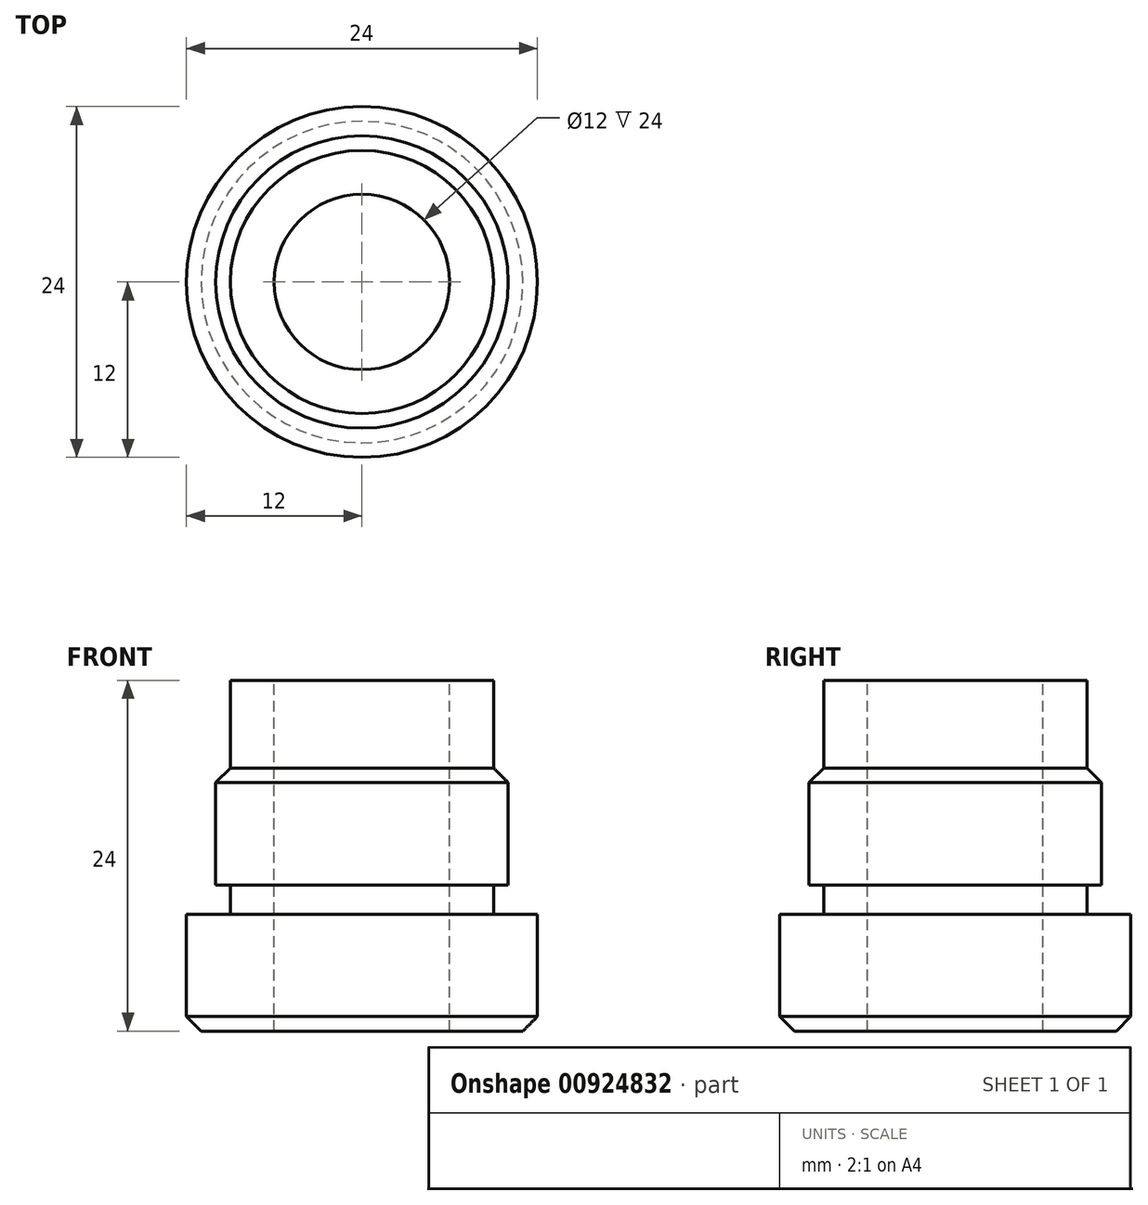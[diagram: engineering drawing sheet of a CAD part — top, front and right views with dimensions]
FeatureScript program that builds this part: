
annotation { "Feature Type Name" : "Feature", "Feature Type Description" : "" }
export const myFeature = defineFeature(function(context is Context, id is Id, definition is map)
    precondition{}
    {
        {
            var Q0;
            Q0=qCreatedBy(makeId("Top.planeOp"),FACE);
            var sketch = newSketch(context, id + "F0", { "sketchPlane" : qUnion([Q0])});
            skCircle(sketch, "E0", {"center": v(0, 0) * mm, "radius": 12 * mm});
            skSolve(sketch);
        }
        {
            var Q0;
            Q0 = qSketchRegion(id + "F0", true);
            extrude(context, id + "F1", {"entities" : qUnion([Q0]), "depth" : 8 * mm, "offsetDistance" : 25 * mm});
        }
        {
            var Q0;
            Q0=makeQuery(id+"F1.opExtrude","CAP_FACE",FACE,{"disambiguationData":[OSD([sQuery(id+"F0.wireOp",EDGE,"E0")])],"isStart":false});
            var sketch = newSketch(context, id + "F2", { "sketchPlane" : qUnion([Q0])});
            skCircle(sketch, "E1", {"center": v(0, 0) * mm, "radius": 10 * mm});
            skSolve(sketch);
        }
        {
            var Q0;
            Q0 = qSketchRegion(id + "F2", true);
            extrude(context, id + "F3", {"entities" : qUnion([Q0]), "operationType" : NewBodyOperationType.ADD, "depth" : 10 * mm, "offsetDistance" : 25 * mm});
        }
        {
            var Q0;
            Q0=makeQuery(id+"F3.opExtrude","CAP_FACE",FACE,{"disambiguationData":[OSD([sQuery(id+"F2.wireOp",EDGE,"E1")])],"isStart":false});
            var sketch = newSketch(context, id + "F4", { "sketchPlane" : qUnion([Q0])});
            skCircle(sketch, "E2", {"center": v(0, 0) * mm, "radius": 9 * mm});
            skSolve(sketch);
        }
        {
            var Q0;
            Q0 = qSketchRegion(id + "F4", true);
            extrude(context, id + "F5", {"entities" : qUnion([Q0]), "operationType" : NewBodyOperationType.ADD, "depth" : 6 * mm, "offsetDistance" : 25 * mm});
        }
        {
            var Q0;
            Q0=qCreatedBy(makeId("Right.planeOp"),FACE);
            var sketch = newSketch(context, id + "F6", { "sketchPlane" : qUnion([Q0])});
            skLineSegment(sketch, "E3.bottom", {"start": v(10, 8) * mm, "end": v(9, 8) * mm});
            skLineSegment(sketch, "E3.top", {"start": v(10, 10) * mm, "end": v(9, 10) * mm});
            skLineSegment(sketch, "E3.left", {"start": v(10, 8) * mm, "end": v(10, 10) * mm});
            skLineSegment(sketch, "E3.right", {"start": v(9, 8) * mm, "end": v(9, 10) * mm});
            skSolve(sketch);
        }
        {
            var Q0;
            Q0=qCreatedBy(makeId("Front.planeOp"),FACE);
            var sketch = newSketch(context, id + "F7", { "sketchPlane" : qUnion([Q0])});
            skLineSegment(sketch, "E4", {"start": v(0, 0) * mm, "end": v(0, 27.45) * mm, "construction": true});
            skSolve(sketch);
        }
        {
            var Q0;
            Q0 = qSketchRegion(id + "F6", true);
            var Q1;
            Q1=sQuery(id+"F7.wireOp",EDGE,"E4");
            revolve(context, id + "F8", {"operationType" : NewBodyOperationType.REMOVE, "surfaceOperationType" : NewSurfaceOperationType.NEW, "entities" : qUnion([Q0]), "axis" : qUnion([Q1]), "revolveType" : RevolveType.FULL, "oppositeDirection" : true});
        }
        {
            var Q0;
            Q0=makeQuery(id+"F1.opExtrude","CAP_EDGE",EDGE,{"disambiguationData":[OSD([sQuery(id+"F0.wireOp",EDGE,"E0")])],"isStart":true});
            chamfer(context, id + "F9", {"entities" : qUnion([Q0]), "width" : 1 * mm, "tangentPropagation" : true});
        }
        {
            var Q0;
            Q0=makeQuery(id+"F3.opExtrude","CAP_EDGE",EDGE,{"disambiguationData":[OSD([sQuery(id+"F2.wireOp",EDGE,"E1")])],"isStart":false});
            chamfer(context, id + "F10", {"entities" : qUnion([Q0]), "width" : 1 * mm, "tangentPropagation" : true});
        }
        {
            var Q0;
            Q0=makeQuery(id+"F5.opExtrude","CAP_FACE",FACE,{"disambiguationData":[OSD([sQuery(id+"F4.wireOp",EDGE,"E2")])],"isStart":false});
            var sketch = newSketch(context, id + "F11", { "sketchPlane" : qUnion([Q0])});
            skCircle(sketch, "E5", {"center": v(0, 0) * mm, "radius": 6 * mm});
            skSolve(sketch);
        }
        {
            var Q0;
            Q0 = qSketchRegion(id + "F11", true);
            extrude(context, id + "F12", {"entities" : qUnion([Q0]), "operationType" : NewBodyOperationType.REMOVE, "oppositeDirection" : true, "depth" : 42.1 * mm, "offsetDistance" : 25 * mm});
        }
    });
